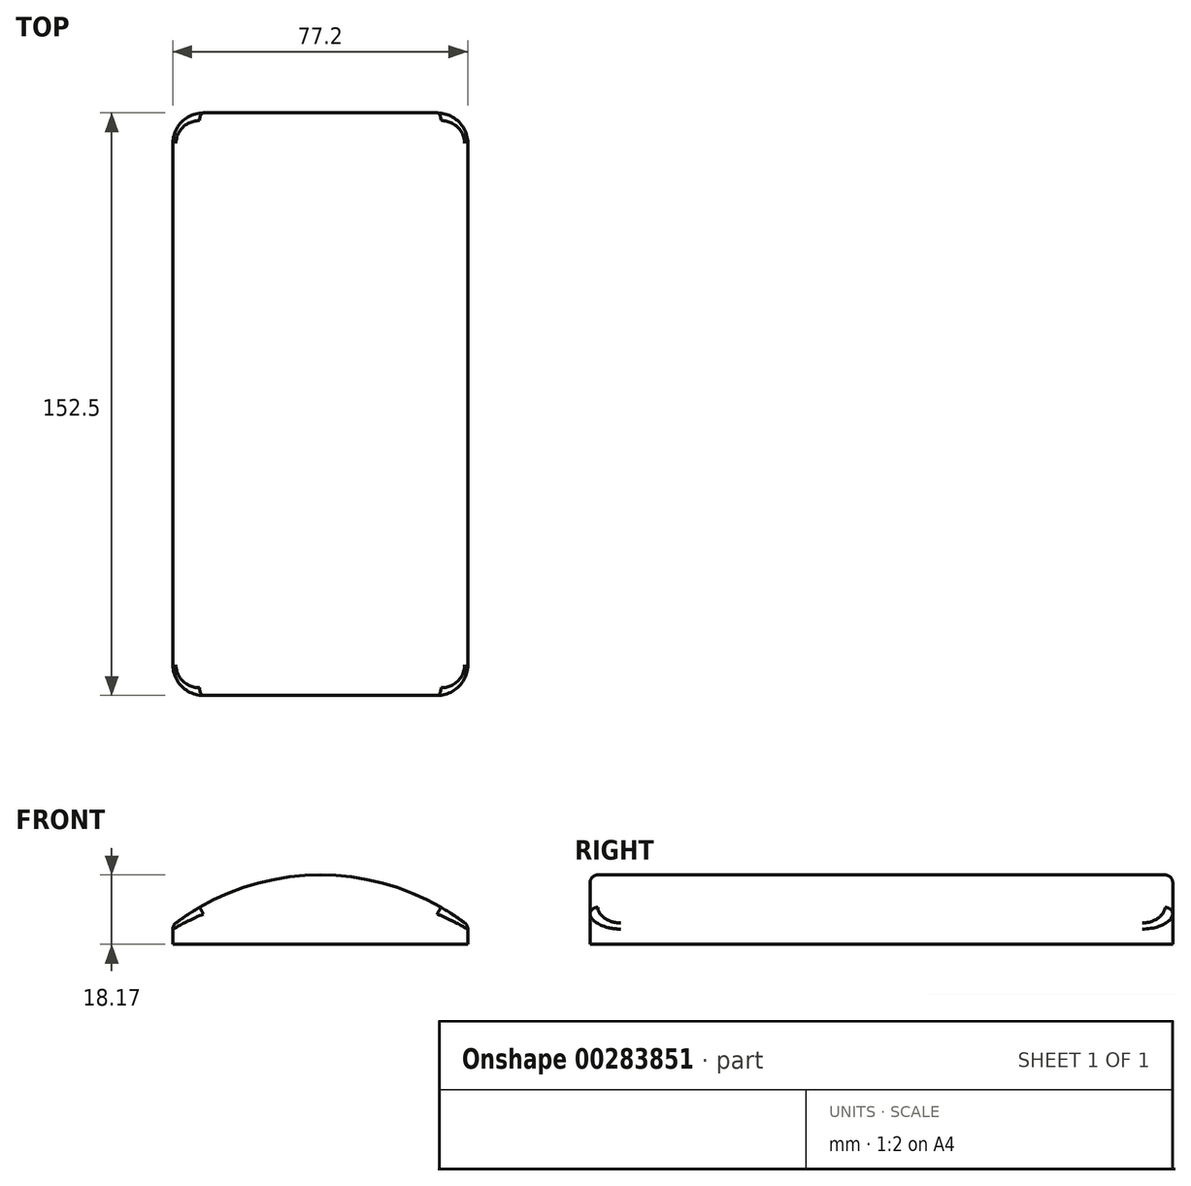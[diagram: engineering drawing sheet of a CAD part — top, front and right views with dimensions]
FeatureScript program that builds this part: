
annotation { "Feature Type Name" : "Feature", "Feature Type Description" : "" }
export const myFeature = defineFeature(function(context is Context, id is Id, definition is map)
    precondition{}
    {
        {
            var Q0;
            Q0=qCreatedBy(makeId("Top.planeOp"),FACE);
            var sketch = newSketch(context, id + "F0", { "sketchPlane" : qUnion([Q0])});
            skLineSegment(sketch, "E0.bottom", {"start": v(-38.6, 76.25) * mm, "end": v(38.6, 76.25) * mm});
            skLineSegment(sketch, "E0.top", {"start": v(-38.6, -76.25) * mm, "end": v(38.6, -76.25) * mm});
            skLineSegment(sketch, "E0.left", {"start": v(-38.6, 76.25) * mm, "end": v(-38.6, -76.25) * mm});
            skLineSegment(sketch, "E0.right", {"start": v(38.6, 76.25) * mm, "end": v(38.6, -76.25) * mm});
            skPoint(sketch, "E0.middle", {"position": v(0, 0) * mm});
            skLineSegment(sketch, "E1", {"start": v(38.6, 0) * mm, "end": v(0, 0) * mm, "construction": true});
            skLineSegment(sketch, "E2", {"start": v(0, -76.25) * mm, "end": v(0, 0) * mm, "construction": true});
            skSolve(sketch);
        }
        {
            var Q0;
            Q0 = qSketchRegion(id + "F0", true);
            extrude(context, id + "F1", {"entities" : qUnion([Q0]), "depth" : 5 * mm});
        }
        {
            var Q0;
            Q0=makeQuery(id+"F1.opExtrude","SWEPT_FACE",FACE,{"disambiguationData":[OSD([sQuery(id+"F0.wireOp",EDGE,"E0.top")])]});
            var sketch = newSketch(context, id + "F2", { "sketchPlane" : qUnion([Q0])});
            skLineSegment(sketch, "E3", {"start": v(-38.6, 5) * mm, "end": v(38.6, 5) * mm});
            skArc(sketch, "E4", {"start": v(38.6, 5) * mm, "mid": v(0, 18.17) * mm, "end": v(-38.6, 5) * mm});
            skLineSegment(sketch, "E5", {"start": v(0, -45) * mm, "end": v(0, 0) * mm, "construction": true});
            skSolve(sketch);
        }
        {
            var Q0;
            Q0 = qSketchRegion(id + "F2", true);
            var Q1;
            Q1=makeQuery(id+"F1.opExtrude","SWEPT_FACE",FACE,{"disambiguationData":[OSD([sQuery(id+"F0.wireOp",EDGE,"E0.bottom")])]});
            extrude(context, id + "F3", {"entities" : qUnion([Q0]), "operationType" : NewBodyOperationType.ADD, "endBound" : BoundingType.UP_TO_SURFACE, "oppositeDirection" : true, "endBoundEntityFace" : qUnion([Q1]), "depth" : 63.17 * mm});
        }
        {
            var Q0;
            Q0=makeQuery(id+"F1.opExtrude","SWEPT_EDGE",EDGE,{"disambiguationData":[OSD([sQuery(id+"F0.wireOp",EDGE,"E0.bottom"),sQuery(id+"F0.wireOp",EDGE,"E0.right")])]});
            var Q1;
            Q1=makeQuery(id+"F1.opExtrude","SWEPT_EDGE",EDGE,{"disambiguationData":[OSD([sQuery(id+"F0.wireOp",EDGE,"E0.bottom"),sQuery(id+"F0.wireOp",EDGE,"E0.left")])]});
            var Q2;
            Q2=makeQuery(id+"F1.opExtrude","SWEPT_EDGE",EDGE,{"disambiguationData":[OSD([sQuery(id+"F0.wireOp",EDGE,"E0.top"),sQuery(id+"F0.wireOp",EDGE,"E0.right")])]});
            var Q3;
            Q3=makeQuery(id+"F1.opExtrude","SWEPT_EDGE",EDGE,{"disambiguationData":[OSD([sQuery(id+"F0.wireOp",EDGE,"E0.top"),sQuery(id+"F0.wireOp",EDGE,"E0.left")])]});
            fillet(context, id + "F4", {"entities" : qUnion([Q0, Q1, Q2, Q3]), "radius" : 8 * mm, "tangentPropagation" : true, "allowEdgeOverflow" : false});
        }
        {
            var Q0;
            Q0=makeQuery(id+"F3.opExtrude","CAP_EDGE",EDGE,{"disambiguationData":[OSD([sQuery(id+"F2.wireOp",EDGE,"E4")])],"isStart":true});
            fillet(context, id + "F5", {"entities" : qUnion([Q0]), "radius" : 2 * mm, "tangentPropagation" : true, "allowEdgeOverflow" : false});
        }
    });
